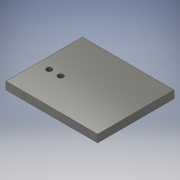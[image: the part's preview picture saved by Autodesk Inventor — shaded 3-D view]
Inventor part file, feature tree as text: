
AUTODESK INVENTOR PART (.ipt)
format: ipt  version: 2019 (Build 230136000, 136)  size: 111,616 bytes
history: native  units: mm
features: extrude x2, thread x2, sketch x2
ambient origin geometry x8: Origin, YZ Plane, XZ Plane, XY Plane, X Axis, Y Axis, Z Axis, Center Point
bodies: Solid1 (feature_tree)
feature tree (6):
  extrude  "Extrusion1"  Depth=120.0mm
  extrude  "Extrusion2"  Depth=10.0mm
  thread  "Thread1"  [1 undecoded]
  thread  "Thread2"  [1 undecoded]
  sketch  "Sketch1"  dims[d0=100.0mm d1=120.0mm]
  sketch  "Sketch2"  dims[d2=70.0mm d3=41.666667mm d4=10.0mm d5=0.0mm d6=7.0mm d7=7.0mm d8=30.0mm d9=15.0mm d12=15.0mm d13=40.0mm d14=5.0mm d15=0.0mm d16=10.0mm d17=0.0mm d18=10.0mm d19=0.0mm]
note: 2 required parameter values undecoded (feature->parameter linkage not recoverable at this tier; creation-order binding heuristic only, values carry confidence <= 0.55)
